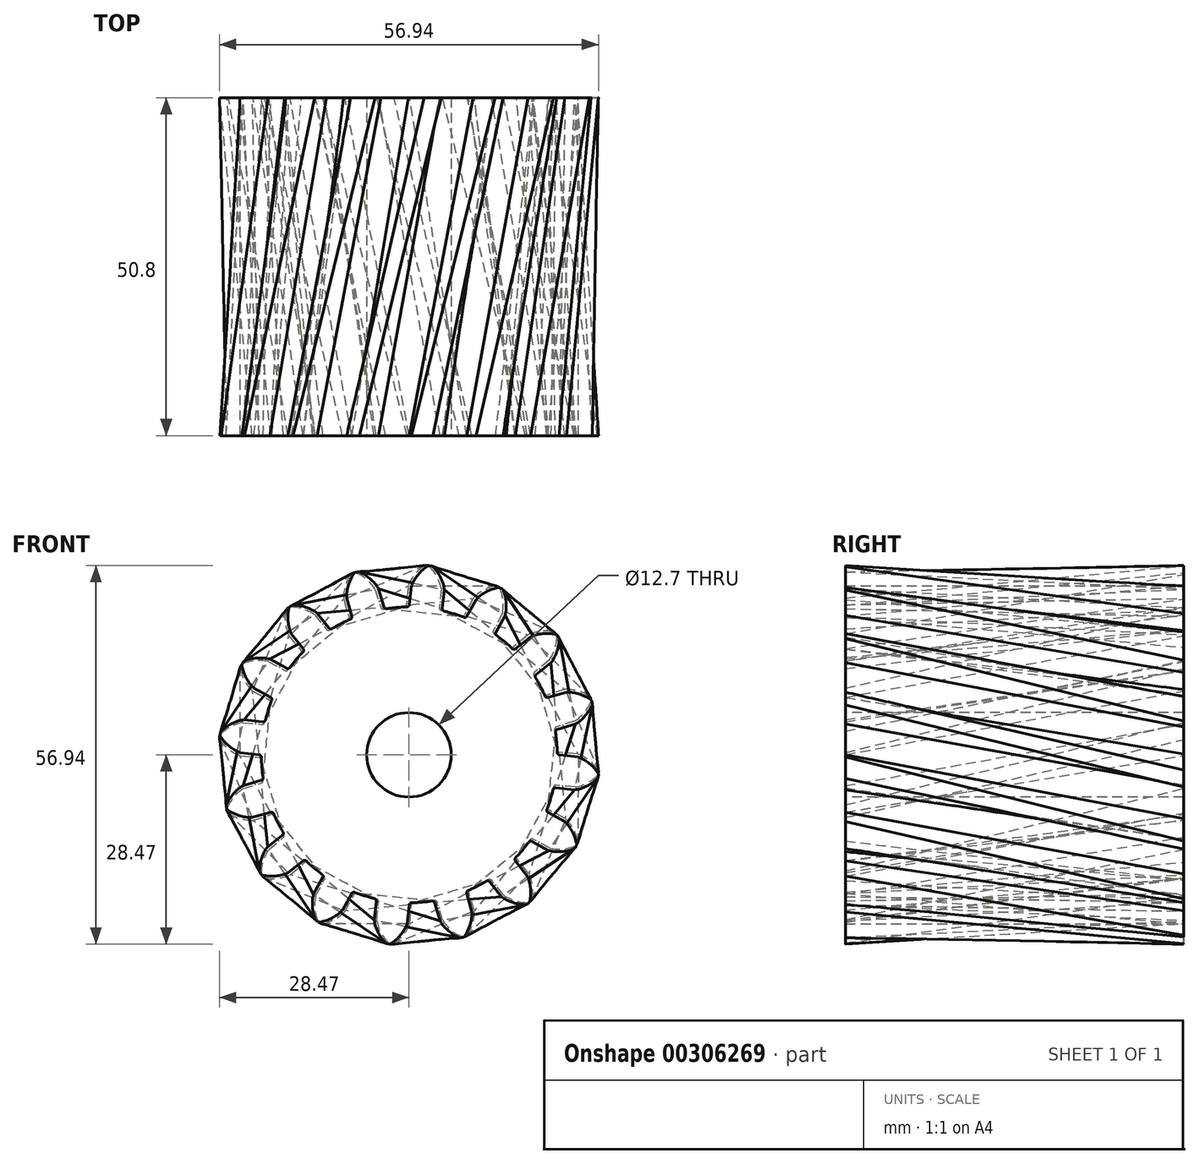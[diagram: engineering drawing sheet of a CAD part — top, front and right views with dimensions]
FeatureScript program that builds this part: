
annotation { "Feature Type Name" : "Feature", "Feature Type Description" : "" }
export const myFeature = defineFeature(function(context is Context, id is Id, definition is map)
    precondition{}
    {
        {
            var Q0;
            Q0=qCreatedBy(makeId("Front.planeOp"),FACE);
            var sketch = newSketch(context, id + "F0", { "sketchPlane" : qUnion([Q0])});
            skArc(sketch, "E0", {"start": v(-0.74, 22.21) * mm, "mid": v(-2.44, 22.1) * mm, "end": v(-4.12, 21.84) * mm});
            skArc(sketch, "E1.trimOffspring", {"start": v(4.85, 24.93) * mm, "mid": v(4.22, 26.77) * mm, "end": v(3.08, 28.32) * mm});
            skLineSegment(sketch, "E2", {"start": v(4.85, 24.93) * mm, "end": v(4.58, 22.1) * mm});
            skLineSegment(sketch, "E3", {"start": v(2.85, 28.43) * mm, "end": v(2.68, 28.45) * mm});
            skArc(sketch, "E4.MirrorCS", {"start": v(-0.11, 25.4) * mm, "mid": v(0.84, 27.08) * mm, "end": v(2.26, 28.4) * mm});
            skLineSegment(sketch, "E5.MirrorCS", {"start": v(2.5, 28.47) * mm, "end": v(2.68, 28.45) * mm});
            skLineSegment(sketch, "E6.MirrorCS", {"start": v(-0.11, 25.4) * mm, "end": v(-0.38, 22.56) * mm});
            skPoint(sketch, "E7.visualSharp", {"position": v(-0.4, 22.22) * mm});
            skArc(sketch, "E7.filletArc", {"start": v(-0.74, 22.21) * mm, "mid": v(-0.5, 22.32) * mm, "end": v(-0.38, 22.56) * mm});
            skPoint(sketch, "E8.visualSharp", {"position": v(4.55, 21.75) * mm});
            skArc(sketch, "E8.filletArc", {"start": v(4.58, 22.1) * mm, "mid": v(4.65, 21.83) * mm, "end": v(4.87, 21.68) * mm});
            skPoint(sketch, "E9.visualSharp", {"position": v(2.98, 28.42) * mm});
            skArc(sketch, "E9.filletArc", {"start": v(3.08, 28.32) * mm, "mid": v(2.97, 28.4) * mm, "end": v(2.85, 28.43) * mm});
            skPoint(sketch, "E10.visualSharp", {"position": v(2.37, 28.48) * mm});
            skArc(sketch, "E10.filletArc", {"start": v(2.5, 28.47) * mm, "mid": v(2.38, 28.45) * mm, "end": v(2.26, 28.4) * mm});
            skLineSegment(sketch, "E11.1.0", {"start": v(-9.82, 23.42) * mm, "end": v(-8.98, 20.7) * mm});
            skPoint(sketch, "E11.1.1", {"position": v(-8.88, 20.37) * mm});
            skLineSegment(sketch, "E11.1.2", {"start": v(-5.06, 24.9) * mm, "end": v(-4.22, 22.16) * mm});
            skPoint(sketch, "E11.1.3", {"position": v(-8.7, 27.22) * mm});
            skArc(sketch, "E11.1.4", {"start": v(-9.82, 23.42) * mm, "mid": v(-9.58, 25.34) * mm, "end": v(-8.78, 27.1) * mm});
            skPoint(sketch, "E11.1.5", {"position": v(-4.12, 21.84) * mm});
            skArc(sketch, "E11.1.6", {"start": v(-5.06, 24.9) * mm, "mid": v(-6.34, 26.34) * mm, "end": v(-8, 27.35) * mm});
            skPoint(sketch, "E11.1.7", {"position": v(-8.12, 27.4) * mm});
            skArc(sketch, "E11.1.8", {"start": v(-8.58, 27.26) * mm, "mid": v(-8.7, 27.2) * mm, "end": v(-8.78, 27.1) * mm});
            skLineSegment(sketch, "E11.1.9", {"start": v(-8.58, 27.26) * mm, "end": v(-8.41, 27.3) * mm});
            skArc(sketch, "E11.1.10", {"start": v(-9.19, 20.24) * mm, "mid": v(-9, 20.43) * mm, "end": v(-8.98, 20.7) * mm});
            skArc(sketch, "E11.1.11", {"start": v(-4.22, 22.16) * mm, "mid": v(-4.06, 21.95) * mm, "end": v(-3.8, 21.9) * mm});
            skLineSegment(sketch, "E11.1.12", {"start": v(-8.25, 27.36) * mm, "end": v(-8.41, 27.3) * mm});
            skArc(sketch, "E11.1.13", {"start": v(-8, 27.35) * mm, "mid": v(-8.12, 27.37) * mm, "end": v(-8.25, 27.36) * mm});
            skLineSegment(sketch, "E11.2.0", {"start": v(-18.04, 17.88) * mm, "end": v(-16.22, 15.68) * mm});
            skPoint(sketch, "E11.2.1", {"position": v(-16, 15.42) * mm});
            skLineSegment(sketch, "E11.2.2", {"start": v(-14.2, 21.06) * mm, "end": v(-12.38, 18.86) * mm});
            skPoint(sketch, "E11.2.3", {"position": v(-18.46, 21.81) * mm});
            skArc(sketch, "E11.2.4", {"start": v(-18.04, 17.88) * mm, "mid": v(-18.55, 19.75) * mm, "end": v(-18.48, 21.68) * mm});
            skPoint(sketch, "E11.2.5", {"position": v(-12.17, 18.6) * mm});
            skArc(sketch, "E11.2.6", {"start": v(-14.2, 21.06) * mm, "mid": v(-15.94, 21.91) * mm, "end": v(-17.85, 22.2) * mm});
            skPoint(sketch, "E11.2.7", {"position": v(-17.99, 22.2) * mm});
            skArc(sketch, "E11.2.8", {"start": v(-18.36, 21.9) * mm, "mid": v(-18.44, 21.8) * mm, "end": v(-18.48, 21.68) * mm});
            skLineSegment(sketch, "E11.2.9", {"start": v(-18.36, 21.9) * mm, "end": v(-18.23, 22.01) * mm});
            skArc(sketch, "E11.2.10", {"start": v(-16.23, 15.18) * mm, "mid": v(-16.13, 15.43) * mm, "end": v(-16.22, 15.68) * mm});
            skArc(sketch, "E11.2.11", {"start": v(-12.38, 18.86) * mm, "mid": v(-12.15, 18.73) * mm, "end": v(-11.89, 18.78) * mm});
            skLineSegment(sketch, "E11.2.12", {"start": v(-18.1, 22.12) * mm, "end": v(-18.23, 22.01) * mm});
            skArc(sketch, "E11.2.13", {"start": v(-17.85, 22.2) * mm, "mid": v(-17.98, 22.18) * mm, "end": v(-18.1, 22.12) * mm});
            skLineSegment(sketch, "E11.3.0", {"start": v(-23.5, 9.62) * mm, "end": v(-20.99, 8.28) * mm});
            skPoint(sketch, "E11.3.1", {"position": v(-20.69, 8.13) * mm});
            skLineSegment(sketch, "E11.3.2", {"start": v(-21.18, 14.02) * mm, "end": v(-18.66, 12.68) * mm});
            skPoint(sketch, "E11.3.3", {"position": v(-25.4, 13.1) * mm});
            skArc(sketch, "E11.3.4", {"start": v(-23.5, 9.62) * mm, "mid": v(-24.7, 11.14) * mm, "end": v(-25.37, 12.96) * mm});
            skPoint(sketch, "E11.3.5", {"position": v(-18.36, 12.53) * mm});
            skArc(sketch, "E11.3.6", {"start": v(-21.18, 14.02) * mm, "mid": v(-23.11, 14.14) * mm, "end": v(-25, 13.68) * mm});
            skPoint(sketch, "E11.3.7", {"position": v(-25.12, 13.63) * mm});
            skArc(sketch, "E11.3.8", {"start": v(-25.34, 13.2) * mm, "mid": v(-25.38, 13.09) * mm, "end": v(-25.37, 12.96) * mm});
            skLineSegment(sketch, "E11.3.9", {"start": v(-25.34, 13.2) * mm, "end": v(-25.26, 13.36) * mm});
            skArc(sketch, "E11.3.10", {"start": v(-20.8, 7.81) * mm, "mid": v(-20.8, 8.08) * mm, "end": v(-20.99, 8.28) * mm});
            skArc(sketch, "E11.3.11", {"start": v(-18.66, 12.68) * mm, "mid": v(-18.4, 12.65) * mm, "end": v(-18.17, 12.8) * mm});
            skLineSegment(sketch, "E11.3.12", {"start": v(-25.18, 13.51) * mm, "end": v(-25.26, 13.36) * mm});
            skArc(sketch, "E11.3.13", {"start": v(-25, 13.68) * mm, "mid": v(-25.1, 13.61) * mm, "end": v(-25.18, 13.51) * mm});
            skLineSegment(sketch, "E11.4.0", {"start": v(-25.4, -0.11) * mm, "end": v(-22.56, -0.38) * mm});
            skPoint(sketch, "E11.4.1", {"position": v(-22.22, -0.4) * mm});
            skLineSegment(sketch, "E11.4.2", {"start": v(-24.93, 4.85) * mm, "end": v(-22.1, 4.58) * mm});
            skPoint(sketch, "E11.4.3", {"position": v(-28.48, 2.37) * mm});
            skArc(sketch, "E11.4.4", {"start": v(-25.4, -0.11) * mm, "mid": v(-27.08, 0.84) * mm, "end": v(-28.4, 2.26) * mm});
            skPoint(sketch, "E11.4.5", {"position": v(-21.75, 4.55) * mm});
            skArc(sketch, "E11.4.6", {"start": v(-24.93, 4.85) * mm, "mid": v(-26.77, 4.22) * mm, "end": v(-28.32, 3.08) * mm});
            skPoint(sketch, "E11.4.7", {"position": v(-28.42, 2.98) * mm});
            skArc(sketch, "E11.4.8", {"start": v(-28.47, 2.5) * mm, "mid": v(-28.45, 2.38) * mm, "end": v(-28.4, 2.26) * mm});
            skLineSegment(sketch, "E11.4.9", {"start": v(-28.47, 2.5) * mm, "end": v(-28.45, 2.68) * mm});
            skArc(sketch, "E11.4.10", {"start": v(-22.21, -0.74) * mm, "mid": v(-22.32, -0.5) * mm, "end": v(-22.56, -0.38) * mm});
            skArc(sketch, "E11.4.11", {"start": v(-22.1, 4.58) * mm, "mid": v(-21.83, 4.65) * mm, "end": v(-21.68, 4.87) * mm});
            skLineSegment(sketch, "E11.4.12", {"start": v(-28.43, 2.85) * mm, "end": v(-28.45, 2.68) * mm});
            skArc(sketch, "E11.4.13", {"start": v(-28.32, 3.08) * mm, "mid": v(-28.4, 2.97) * mm, "end": v(-28.43, 2.85) * mm});
            skLineSegment(sketch, "E11.5.0", {"start": v(-23.42, -9.82) * mm, "end": v(-20.7, -8.98) * mm});
            skPoint(sketch, "E11.5.1", {"position": v(-20.37, -8.88) * mm});
            skLineSegment(sketch, "E11.5.2", {"start": v(-24.9, -5.06) * mm, "end": v(-22.16, -4.22) * mm});
            skPoint(sketch, "E11.5.3", {"position": v(-27.22, -8.7) * mm});
            skArc(sketch, "E11.5.4", {"start": v(-23.42, -9.82) * mm, "mid": v(-25.34, -9.58) * mm, "end": v(-27.1, -8.78) * mm});
            skPoint(sketch, "E11.5.5", {"position": v(-21.84, -4.12) * mm});
            skArc(sketch, "E11.5.6", {"start": v(-24.9, -5.06) * mm, "mid": v(-26.34, -6.34) * mm, "end": v(-27.35, -8) * mm});
            skPoint(sketch, "E11.5.7", {"position": v(-27.4, -8.12) * mm});
            skArc(sketch, "E11.5.8", {"start": v(-27.26, -8.58) * mm, "mid": v(-27.2, -8.7) * mm, "end": v(-27.1, -8.78) * mm});
            skLineSegment(sketch, "E11.5.9", {"start": v(-27.26, -8.58) * mm, "end": v(-27.3, -8.41) * mm});
            skArc(sketch, "E11.5.10", {"start": v(-20.24, -9.19) * mm, "mid": v(-20.43, -9) * mm, "end": v(-20.7, -8.98) * mm});
            skArc(sketch, "E11.5.11", {"start": v(-22.16, -4.22) * mm, "mid": v(-21.95, -4.06) * mm, "end": v(-21.9, -3.8) * mm});
            skLineSegment(sketch, "E11.5.12", {"start": v(-27.36, -8.25) * mm, "end": v(-27.3, -8.41) * mm});
            skArc(sketch, "E11.5.13", {"start": v(-27.35, -8) * mm, "mid": v(-27.37, -8.12) * mm, "end": v(-27.36, -8.25) * mm});
            skLineSegment(sketch, "E11.6.0", {"start": v(-17.88, -18.04) * mm, "end": v(-15.68, -16.22) * mm});
            skPoint(sketch, "E11.6.1", {"position": v(-15.42, -16) * mm});
            skLineSegment(sketch, "E11.6.2", {"start": v(-21.06, -14.2) * mm, "end": v(-18.86, -12.38) * mm});
            skPoint(sketch, "E11.6.3", {"position": v(-21.81, -18.46) * mm});
            skArc(sketch, "E11.6.4", {"start": v(-17.88, -18.04) * mm, "mid": v(-19.75, -18.55) * mm, "end": v(-21.68, -18.48) * mm});
            skPoint(sketch, "E11.6.5", {"position": v(-18.6, -12.17) * mm});
            skArc(sketch, "E11.6.6", {"start": v(-21.06, -14.2) * mm, "mid": v(-21.91, -15.94) * mm, "end": v(-22.2, -17.85) * mm});
            skPoint(sketch, "E11.6.7", {"position": v(-22.2, -17.99) * mm});
            skArc(sketch, "E11.6.8", {"start": v(-21.9, -18.36) * mm, "mid": v(-21.8, -18.44) * mm, "end": v(-21.68, -18.48) * mm});
            skLineSegment(sketch, "E11.6.9", {"start": v(-21.9, -18.36) * mm, "end": v(-22.01, -18.23) * mm});
            skArc(sketch, "E11.6.10", {"start": v(-15.18, -16.23) * mm, "mid": v(-15.43, -16.13) * mm, "end": v(-15.68, -16.22) * mm});
            skArc(sketch, "E11.6.11", {"start": v(-18.86, -12.38) * mm, "mid": v(-18.73, -12.15) * mm, "end": v(-18.78, -11.89) * mm});
            skLineSegment(sketch, "E11.6.12", {"start": v(-22.12, -18.1) * mm, "end": v(-22.01, -18.23) * mm});
            skArc(sketch, "E11.6.13", {"start": v(-22.2, -17.85) * mm, "mid": v(-22.18, -17.98) * mm, "end": v(-22.12, -18.1) * mm});
            skLineSegment(sketch, "E11.7.0", {"start": v(-9.62, -23.5) * mm, "end": v(-8.28, -20.99) * mm});
            skPoint(sketch, "E11.7.1", {"position": v(-8.13, -20.69) * mm});
            skLineSegment(sketch, "E11.7.2", {"start": v(-14.02, -21.18) * mm, "end": v(-12.68, -18.66) * mm});
            skPoint(sketch, "E11.7.3", {"position": v(-13.1, -25.4) * mm});
            skArc(sketch, "E11.7.4", {"start": v(-9.62, -23.5) * mm, "mid": v(-11.14, -24.7) * mm, "end": v(-12.96, -25.37) * mm});
            skPoint(sketch, "E11.7.5", {"position": v(-12.53, -18.36) * mm});
            skArc(sketch, "E11.7.6", {"start": v(-14.02, -21.18) * mm, "mid": v(-14.14, -23.11) * mm, "end": v(-13.68, -25) * mm});
            skPoint(sketch, "E11.7.7", {"position": v(-13.63, -25.12) * mm});
            skArc(sketch, "E11.7.8", {"start": v(-13.2, -25.34) * mm, "mid": v(-13.09, -25.38) * mm, "end": v(-12.96, -25.37) * mm});
            skLineSegment(sketch, "E11.7.9", {"start": v(-13.2, -25.34) * mm, "end": v(-13.36, -25.26) * mm});
            skArc(sketch, "E11.7.10", {"start": v(-7.81, -20.8) * mm, "mid": v(-8.08, -20.8) * mm, "end": v(-8.28, -20.99) * mm});
            skArc(sketch, "E11.7.11", {"start": v(-12.68, -18.66) * mm, "mid": v(-12.65, -18.4) * mm, "end": v(-12.8, -18.17) * mm});
            skLineSegment(sketch, "E11.7.12", {"start": v(-13.51, -25.18) * mm, "end": v(-13.36, -25.26) * mm});
            skArc(sketch, "E11.7.13", {"start": v(-13.68, -25) * mm, "mid": v(-13.61, -25.1) * mm, "end": v(-13.51, -25.18) * mm});
            skLineSegment(sketch, "E11.8.0", {"start": v(0.11, -25.4) * mm, "end": v(0.38, -22.56) * mm});
            skPoint(sketch, "E11.8.1", {"position": v(0.4, -22.22) * mm});
            skLineSegment(sketch, "E11.8.2", {"start": v(-4.85, -24.93) * mm, "end": v(-4.58, -22.1) * mm});
            skPoint(sketch, "E11.8.3", {"position": v(-2.37, -28.48) * mm});
            skArc(sketch, "E11.8.4", {"start": v(0.11, -25.4) * mm, "mid": v(-0.84, -27.08) * mm, "end": v(-2.26, -28.4) * mm});
            skPoint(sketch, "E11.8.5", {"position": v(-4.55, -21.75) * mm});
            skArc(sketch, "E11.8.6", {"start": v(-4.85, -24.93) * mm, "mid": v(-4.22, -26.77) * mm, "end": v(-3.08, -28.32) * mm});
            skPoint(sketch, "E11.8.7", {"position": v(-2.98, -28.42) * mm});
            skArc(sketch, "E11.8.8", {"start": v(-2.5, -28.47) * mm, "mid": v(-2.38, -28.45) * mm, "end": v(-2.26, -28.4) * mm});
            skLineSegment(sketch, "E11.8.9", {"start": v(-2.5, -28.47) * mm, "end": v(-2.68, -28.45) * mm});
            skArc(sketch, "E11.8.10", {"start": v(0.74, -22.21) * mm, "mid": v(0.5, -22.32) * mm, "end": v(0.38, -22.56) * mm});
            skArc(sketch, "E11.8.11", {"start": v(-4.58, -22.1) * mm, "mid": v(-4.65, -21.83) * mm, "end": v(-4.87, -21.68) * mm});
            skLineSegment(sketch, "E11.8.12", {"start": v(-2.85, -28.43) * mm, "end": v(-2.68, -28.45) * mm});
            skArc(sketch, "E11.8.13", {"start": v(-3.08, -28.32) * mm, "mid": v(-2.97, -28.4) * mm, "end": v(-2.85, -28.43) * mm});
            skLineSegment(sketch, "E11.9.0", {"start": v(9.82, -23.42) * mm, "end": v(8.98, -20.7) * mm});
            skPoint(sketch, "E11.9.1", {"position": v(8.88, -20.37) * mm});
            skLineSegment(sketch, "E11.9.2", {"start": v(5.06, -24.9) * mm, "end": v(4.22, -22.16) * mm});
            skPoint(sketch, "E11.9.3", {"position": v(8.7, -27.22) * mm});
            skArc(sketch, "E11.9.4", {"start": v(9.82, -23.42) * mm, "mid": v(9.58, -25.34) * mm, "end": v(8.78, -27.1) * mm});
            skPoint(sketch, "E11.9.5", {"position": v(4.12, -21.84) * mm});
            skArc(sketch, "E11.9.6", {"start": v(5.06, -24.9) * mm, "mid": v(6.34, -26.34) * mm, "end": v(8, -27.35) * mm});
            skPoint(sketch, "E11.9.7", {"position": v(8.12, -27.4) * mm});
            skArc(sketch, "E11.9.8", {"start": v(8.58, -27.26) * mm, "mid": v(8.7, -27.2) * mm, "end": v(8.78, -27.1) * mm});
            skLineSegment(sketch, "E11.9.9", {"start": v(8.58, -27.26) * mm, "end": v(8.41, -27.3) * mm});
            skArc(sketch, "E11.9.10", {"start": v(9.19, -20.24) * mm, "mid": v(9, -20.43) * mm, "end": v(8.98, -20.7) * mm});
            skArc(sketch, "E11.9.11", {"start": v(4.22, -22.16) * mm, "mid": v(4.06, -21.95) * mm, "end": v(3.8, -21.9) * mm});
            skLineSegment(sketch, "E11.9.12", {"start": v(8.25, -27.36) * mm, "end": v(8.41, -27.3) * mm});
            skArc(sketch, "E11.9.13", {"start": v(8, -27.35) * mm, "mid": v(8.12, -27.37) * mm, "end": v(8.25, -27.36) * mm});
            skLineSegment(sketch, "E11.10.0", {"start": v(18.04, -17.88) * mm, "end": v(16.22, -15.68) * mm});
            skPoint(sketch, "E11.10.1", {"position": v(16, -15.42) * mm});
            skLineSegment(sketch, "E11.10.2", {"start": v(14.2, -21.06) * mm, "end": v(12.38, -18.86) * mm});
            skPoint(sketch, "E11.10.3", {"position": v(18.46, -21.81) * mm});
            skArc(sketch, "E11.10.4", {"start": v(18.04, -17.88) * mm, "mid": v(18.55, -19.75) * mm, "end": v(18.48, -21.68) * mm});
            skPoint(sketch, "E11.10.5", {"position": v(12.17, -18.6) * mm});
            skArc(sketch, "E11.10.6", {"start": v(14.2, -21.06) * mm, "mid": v(15.94, -21.91) * mm, "end": v(17.85, -22.2) * mm});
            skPoint(sketch, "E11.10.7", {"position": v(17.99, -22.2) * mm});
            skArc(sketch, "E11.10.8", {"start": v(18.36, -21.9) * mm, "mid": v(18.44, -21.8) * mm, "end": v(18.48, -21.68) * mm});
            skLineSegment(sketch, "E11.10.9", {"start": v(18.36, -21.9) * mm, "end": v(18.23, -22.01) * mm});
            skArc(sketch, "E11.10.10", {"start": v(16.23, -15.18) * mm, "mid": v(16.13, -15.43) * mm, "end": v(16.22, -15.68) * mm});
            skArc(sketch, "E11.10.11", {"start": v(12.38, -18.86) * mm, "mid": v(12.15, -18.73) * mm, "end": v(11.89, -18.78) * mm});
            skLineSegment(sketch, "E11.10.12", {"start": v(18.1, -22.12) * mm, "end": v(18.23, -22.01) * mm});
            skArc(sketch, "E11.10.13", {"start": v(17.85, -22.2) * mm, "mid": v(17.98, -22.18) * mm, "end": v(18.1, -22.12) * mm});
            skLineSegment(sketch, "E11.11.0", {"start": v(23.5, -9.62) * mm, "end": v(20.99, -8.28) * mm});
            skPoint(sketch, "E11.11.1", {"position": v(20.69, -8.13) * mm});
            skLineSegment(sketch, "E11.11.2", {"start": v(21.18, -14.02) * mm, "end": v(18.66, -12.68) * mm});
            skPoint(sketch, "E11.11.3", {"position": v(25.4, -13.1) * mm});
            skArc(sketch, "E11.11.4", {"start": v(23.5, -9.62) * mm, "mid": v(24.7, -11.14) * mm, "end": v(25.37, -12.96) * mm});
            skPoint(sketch, "E11.11.5", {"position": v(18.36, -12.53) * mm});
            skArc(sketch, "E11.11.6", {"start": v(21.18, -14.02) * mm, "mid": v(23.11, -14.14) * mm, "end": v(25, -13.68) * mm});
            skPoint(sketch, "E11.11.7", {"position": v(25.12, -13.63) * mm});
            skArc(sketch, "E11.11.8", {"start": v(25.34, -13.2) * mm, "mid": v(25.38, -13.09) * mm, "end": v(25.37, -12.96) * mm});
            skLineSegment(sketch, "E11.11.9", {"start": v(25.34, -13.2) * mm, "end": v(25.26, -13.36) * mm});
            skArc(sketch, "E11.11.10", {"start": v(20.8, -7.81) * mm, "mid": v(20.8, -8.08) * mm, "end": v(20.99, -8.28) * mm});
            skArc(sketch, "E11.11.11", {"start": v(18.66, -12.68) * mm, "mid": v(18.4, -12.65) * mm, "end": v(18.17, -12.8) * mm});
            skLineSegment(sketch, "E11.11.12", {"start": v(25.18, -13.51) * mm, "end": v(25.26, -13.36) * mm});
            skArc(sketch, "E11.11.13", {"start": v(25, -13.68) * mm, "mid": v(25.1, -13.61) * mm, "end": v(25.18, -13.51) * mm});
            skLineSegment(sketch, "E11.12.0", {"start": v(25.4, 0.11) * mm, "end": v(22.56, 0.38) * mm});
            skPoint(sketch, "E11.12.1", {"position": v(22.22, 0.4) * mm});
            skLineSegment(sketch, "E11.12.2", {"start": v(24.93, -4.85) * mm, "end": v(22.1, -4.58) * mm});
            skPoint(sketch, "E11.12.3", {"position": v(28.48, -2.37) * mm});
            skArc(sketch, "E11.12.4", {"start": v(25.4, 0.11) * mm, "mid": v(27.08, -0.84) * mm, "end": v(28.4, -2.26) * mm});
            skPoint(sketch, "E11.12.5", {"position": v(21.75, -4.55) * mm});
            skArc(sketch, "E11.12.6", {"start": v(24.93, -4.85) * mm, "mid": v(26.77, -4.22) * mm, "end": v(28.32, -3.08) * mm});
            skPoint(sketch, "E11.12.7", {"position": v(28.42, -2.98) * mm});
            skArc(sketch, "E11.12.8", {"start": v(28.47, -2.5) * mm, "mid": v(28.45, -2.38) * mm, "end": v(28.4, -2.26) * mm});
            skLineSegment(sketch, "E11.12.9", {"start": v(28.47, -2.5) * mm, "end": v(28.45, -2.68) * mm});
            skArc(sketch, "E11.12.10", {"start": v(22.21, 0.74) * mm, "mid": v(22.32, 0.5) * mm, "end": v(22.56, 0.38) * mm});
            skArc(sketch, "E11.12.11", {"start": v(22.1, -4.58) * mm, "mid": v(21.83, -4.65) * mm, "end": v(21.68, -4.87) * mm});
            skLineSegment(sketch, "E11.12.12", {"start": v(28.43, -2.85) * mm, "end": v(28.45, -2.68) * mm});
            skArc(sketch, "E11.12.13", {"start": v(28.32, -3.08) * mm, "mid": v(28.4, -2.97) * mm, "end": v(28.43, -2.85) * mm});
            skLineSegment(sketch, "E11.13.0", {"start": v(23.42, 9.82) * mm, "end": v(20.7, 8.98) * mm});
            skPoint(sketch, "E11.13.1", {"position": v(20.37, 8.88) * mm});
            skLineSegment(sketch, "E11.13.2", {"start": v(24.9, 5.06) * mm, "end": v(22.16, 4.22) * mm});
            skPoint(sketch, "E11.13.3", {"position": v(27.22, 8.7) * mm});
            skArc(sketch, "E11.13.4", {"start": v(23.42, 9.82) * mm, "mid": v(25.34, 9.58) * mm, "end": v(27.1, 8.78) * mm});
            skPoint(sketch, "E11.13.5", {"position": v(21.84, 4.12) * mm});
            skArc(sketch, "E11.13.6", {"start": v(24.9, 5.06) * mm, "mid": v(26.34, 6.34) * mm, "end": v(27.35, 8) * mm});
            skPoint(sketch, "E11.13.7", {"position": v(27.4, 8.12) * mm});
            skArc(sketch, "E11.13.8", {"start": v(27.26, 8.58) * mm, "mid": v(27.2, 8.7) * mm, "end": v(27.1, 8.78) * mm});
            skLineSegment(sketch, "E11.13.9", {"start": v(27.26, 8.58) * mm, "end": v(27.3, 8.41) * mm});
            skArc(sketch, "E11.13.10", {"start": v(20.24, 9.19) * mm, "mid": v(20.43, 9) * mm, "end": v(20.7, 8.98) * mm});
            skArc(sketch, "E11.13.11", {"start": v(22.16, 4.22) * mm, "mid": v(21.95, 4.06) * mm, "end": v(21.9, 3.8) * mm});
            skLineSegment(sketch, "E11.13.12", {"start": v(27.36, 8.25) * mm, "end": v(27.3, 8.41) * mm});
            skArc(sketch, "E11.13.13", {"start": v(27.35, 8) * mm, "mid": v(27.37, 8.12) * mm, "end": v(27.36, 8.25) * mm});
            skLineSegment(sketch, "E11.14.0", {"start": v(17.88, 18.04) * mm, "end": v(15.68, 16.22) * mm});
            skPoint(sketch, "E11.14.1", {"position": v(15.42, 16) * mm});
            skLineSegment(sketch, "E11.14.2", {"start": v(21.06, 14.2) * mm, "end": v(18.86, 12.38) * mm});
            skPoint(sketch, "E11.14.3", {"position": v(21.81, 18.46) * mm});
            skArc(sketch, "E11.14.4", {"start": v(17.88, 18.04) * mm, "mid": v(19.75, 18.55) * mm, "end": v(21.68, 18.48) * mm});
            skPoint(sketch, "E11.14.5", {"position": v(18.6, 12.17) * mm});
            skArc(sketch, "E11.14.6", {"start": v(21.06, 14.2) * mm, "mid": v(21.91, 15.94) * mm, "end": v(22.2, 17.85) * mm});
            skPoint(sketch, "E11.14.7", {"position": v(22.2, 17.99) * mm});
            skArc(sketch, "E11.14.8", {"start": v(21.9, 18.36) * mm, "mid": v(21.8, 18.44) * mm, "end": v(21.68, 18.48) * mm});
            skLineSegment(sketch, "E11.14.9", {"start": v(21.9, 18.36) * mm, "end": v(22.01, 18.23) * mm});
            skArc(sketch, "E11.14.10", {"start": v(15.18, 16.23) * mm, "mid": v(15.43, 16.13) * mm, "end": v(15.68, 16.22) * mm});
            skArc(sketch, "E11.14.11", {"start": v(18.86, 12.38) * mm, "mid": v(18.73, 12.15) * mm, "end": v(18.78, 11.89) * mm});
            skLineSegment(sketch, "E11.14.12", {"start": v(22.12, 18.1) * mm, "end": v(22.01, 18.23) * mm});
            skArc(sketch, "E11.14.13", {"start": v(22.2, 17.85) * mm, "mid": v(22.18, 17.98) * mm, "end": v(22.12, 18.1) * mm});
            skLineSegment(sketch, "E11.15.0", {"start": v(9.62, 23.5) * mm, "end": v(8.28, 20.99) * mm});
            skPoint(sketch, "E11.15.1", {"position": v(8.13, 20.69) * mm});
            skLineSegment(sketch, "E11.15.2", {"start": v(14.02, 21.18) * mm, "end": v(12.68, 18.66) * mm});
            skPoint(sketch, "E11.15.3", {"position": v(13.1, 25.4) * mm});
            skArc(sketch, "E11.15.4", {"start": v(9.62, 23.5) * mm, "mid": v(11.14, 24.7) * mm, "end": v(12.96, 25.37) * mm});
            skPoint(sketch, "E11.15.5", {"position": v(12.53, 18.36) * mm});
            skArc(sketch, "E11.15.6", {"start": v(14.02, 21.18) * mm, "mid": v(14.14, 23.11) * mm, "end": v(13.68, 25) * mm});
            skPoint(sketch, "E11.15.7", {"position": v(13.63, 25.12) * mm});
            skArc(sketch, "E11.15.8", {"start": v(13.2, 25.34) * mm, "mid": v(13.09, 25.38) * mm, "end": v(12.96, 25.37) * mm});
            skLineSegment(sketch, "E11.15.9", {"start": v(13.2, 25.34) * mm, "end": v(13.36, 25.26) * mm});
            skArc(sketch, "E11.15.10", {"start": v(7.81, 20.8) * mm, "mid": v(8.08, 20.8) * mm, "end": v(8.28, 20.99) * mm});
            skArc(sketch, "E11.15.11", {"start": v(12.68, 18.66) * mm, "mid": v(12.65, 18.4) * mm, "end": v(12.8, 18.17) * mm});
            skLineSegment(sketch, "E11.15.12", {"start": v(13.51, 25.18) * mm, "end": v(13.36, 25.26) * mm});
            skArc(sketch, "E11.15.13", {"start": v(13.68, 25) * mm, "mid": v(13.61, 25.1) * mm, "end": v(13.51, 25.18) * mm});
            skArc(sketch, "E12.trimOffspring", {"start": v(8.13, 20.69) * mm, "mid": v(6.52, 21.25) * mm, "end": v(4.87, 21.68) * mm});
            skArc(sketch, "E13.trimOffspring", {"start": v(-8.88, 20.37) * mm, "mid": v(-10.56, 19.55) * mm, "end": v(-12.17, 18.6) * mm});
            skArc(sketch, "E14.trimOffspring", {"start": v(15.42, 16) * mm, "mid": v(14.02, 17.24) * mm, "end": v(12.53, 18.36) * mm});
            skArc(sketch, "E15.trimOffspring", {"start": v(-16, 15.42) * mm, "mid": v(-17.24, 14.02) * mm, "end": v(-18.36, 12.53) * mm});
            skArc(sketch, "E16.trimOffspring", {"start": v(-20.69, 8.13) * mm, "mid": v(-21.25, 6.52) * mm, "end": v(-21.68, 4.87) * mm});
            skArc(sketch, "E17.trimOffspring", {"start": v(20.37, 8.88) * mm, "mid": v(19.55, 10.56) * mm, "end": v(18.6, 12.17) * mm});
            skArc(sketch, "E18.trimOffspring", {"start": v(22.22, 0.4) * mm, "mid": v(22.1, 2.27) * mm, "end": v(21.84, 4.12) * mm});
            skArc(sketch, "E19.trimOffspring", {"start": v(-22.22, -0.4) * mm, "mid": v(-22.12, -2.1) * mm, "end": v(-21.9, -3.8) * mm});
            skArc(sketch, "E20.trimOffspring", {"start": v(-20.37, -8.88) * mm, "mid": v(-19.55, -10.56) * mm, "end": v(-18.6, -12.17) * mm});
            skArc(sketch, "E21.trimOffspring", {"start": v(-8.13, -20.69) * mm, "mid": v(-6.36, -21.3) * mm, "end": v(-4.55, -21.75) * mm});
            skArc(sketch, "E22.trimOffspring", {"start": v(-15.42, -16) * mm, "mid": v(-14.02, -17.24) * mm, "end": v(-12.53, -18.36) * mm});
            skArc(sketch, "E23.trimOffspring", {"start": v(0.4, -22.22) * mm, "mid": v(2.1, -22.12) * mm, "end": v(3.8, -21.9) * mm});
            skArc(sketch, "E24.trimOffspring", {"start": v(8.88, -20.37) * mm, "mid": v(10.41, -19.63) * mm, "end": v(11.89, -18.78) * mm});
            skArc(sketch, "E25.trimOffspring", {"start": v(16, -15.42) * mm, "mid": v(17.24, -14.02) * mm, "end": v(18.36, -12.53) * mm});
            skArc(sketch, "E26.trimOffspring", {"start": v(20.69, -8.13) * mm, "mid": v(21.3, -6.36) * mm, "end": v(21.75, -4.55) * mm});
            skSolve(sketch);
        }
        {
            var Q0;
            Q0=makeQuery(id+"F0.imprint","IMPRINT",FACE,{"disambiguationData":[TD([[makeQuery(id+"F0.imprint","IMPRINT",EDGE,{"derivedFrom":sQuery(id+"F0.wireOp",EDGE,"E1.trimOffspring")}),1.0]])]});
            cPlane(context, id + "F1", {"entities" : qUnion([Q0]), "cplaneType" : CPlaneType.OFFSET, "offset" : 50.8 * mm, "width" : 152.4 * mm, "height" : 152.4 * mm});
        }
        {
            var Q0;
            Q0=qCreatedBy(id+"F1.planeOp",FACE);
            var sketch = newSketch(context, id + "F2", { "sketchPlane" : qUnion([Q0])});
            skArc(sketch, "E27", {"start": v(-15.92, 15.46) * mm, "mid": v(-17.06, 14.2) * mm, "end": v(-18.1, 12.85) * mm});
            skArc(sketch, "E28.trimOffspring", {"start": v(-13.79, 21.3) * mm, "mid": v(-15.5, 22.19) * mm, "end": v(-17.42, 22.51) * mm});
            skLineSegment(sketch, "E29", {"start": v(-13.79, 21.3) * mm, "end": v(-12, 19.07) * mm});
            skLineSegment(sketch, "E30", {"start": v(-17.66, 22.43) * mm, "end": v(-17.8, 22.33) * mm});
            skArc(sketch, "E31.MirrorCS", {"start": v(-17.68, 18.2) * mm, "mid": v(-18.16, 20.07) * mm, "end": v(-18.06, 22) * mm});
            skLineSegment(sketch, "E32.MirrorCS", {"start": v(-17.92, 22.22) * mm, "end": v(-17.8, 22.33) * mm});
            skLineSegment(sketch, "E33.MirrorCS", {"start": v(-17.68, 18.2) * mm, "end": v(-15.9, 15.96) * mm});
            skPoint(sketch, "E34.visualSharp", {"position": v(-15.68, 15.7) * mm});
            skArc(sketch, "E34.filletArc", {"start": v(-15.92, 15.46) * mm, "mid": v(-15.81, 15.7) * mm, "end": v(-15.9, 15.96) * mm});
            skPoint(sketch, "E35.visualSharp", {"position": v(-11.8, 18.8) * mm});
            skArc(sketch, "E35.filletArc", {"start": v(-12, 19.07) * mm, "mid": v(-11.77, 18.93) * mm, "end": v(-11.5, 18.98) * mm});
            skPoint(sketch, "E36.visualSharp", {"position": v(-17.55, 22.51) * mm});
            skArc(sketch, "E36.filletArc", {"start": v(-17.42, 22.51) * mm, "mid": v(-17.54, 22.5) * mm, "end": v(-17.66, 22.43) * mm});
            skPoint(sketch, "E37.visualSharp", {"position": v(-18.03, 22.13) * mm});
            skArc(sketch, "E37.filletArc", {"start": v(-17.92, 22.22) * mm, "mid": v(-18, 22.12) * mm, "end": v(-18.06, 22) * mm});
            skLineSegment(sketch, "E38.1.0", {"start": v(-23.3, 10.03) * mm, "end": v(-20.8, 8.65) * mm});
            skPoint(sketch, "E38.1.1", {"position": v(-20.5, 8.48) * mm});
            skLineSegment(sketch, "E38.1.2", {"start": v(-20.89, 14.39) * mm, "end": v(-18.39, 13) * mm});
            skPoint(sketch, "E38.1.3", {"position": v(-25.12, 13.53) * mm});
            skArc(sketch, "E38.1.4", {"start": v(-23.3, 10.03) * mm, "mid": v(-24.45, 11.57) * mm, "end": v(-25.1, 13.4) * mm});
            skPoint(sketch, "E38.1.5", {"position": v(-18.1, 12.85) * mm});
            skArc(sketch, "E38.1.6", {"start": v(-20.89, 14.39) * mm, "mid": v(-22.81, 14.55) * mm, "end": v(-24.7, 14.12) * mm});
            skPoint(sketch, "E38.1.7", {"position": v(-24.83, 14.06) * mm});
            skArc(sketch, "E38.1.8", {"start": v(-25.06, 13.65) * mm, "mid": v(-25.1, 13.53) * mm, "end": v(-25.1, 13.4) * mm});
            skLineSegment(sketch, "E38.1.9", {"start": v(-25.06, 13.65) * mm, "end": v(-24.98, 13.8) * mm});
            skArc(sketch, "E38.1.10", {"start": v(-20.62, 8.17) * mm, "mid": v(-20.62, 8.44) * mm, "end": v(-20.8, 8.65) * mm});
            skArc(sketch, "E38.1.11", {"start": v(-18.39, 13) * mm, "mid": v(-18.12, 12.97) * mm, "end": v(-17.9, 13.12) * mm});
            skLineSegment(sketch, "E38.1.12", {"start": v(-24.9, 13.95) * mm, "end": v(-24.98, 13.8) * mm});
            skArc(sketch, "E38.1.13", {"start": v(-24.7, 14.12) * mm, "mid": v(-24.81, 14.05) * mm, "end": v(-24.9, 13.95) * mm});
            skLineSegment(sketch, "E38.2.0", {"start": v(-25.35, 0.33) * mm, "end": v(-22.51, 0.02) * mm});
            skPoint(sketch, "E38.2.1", {"position": v(-22.18, -0.02) * mm});
            skLineSegment(sketch, "E38.2.2", {"start": v(-24.8, 5.28) * mm, "end": v(-21.96, 4.96) * mm});
            skPoint(sketch, "E38.2.3", {"position": v(-28.38, 2.87) * mm});
            skArc(sketch, "E38.2.4", {"start": v(-25.35, 0.33) * mm, "mid": v(-27.02, 1.32) * mm, "end": v(-28.31, 2.76) * mm});
            skPoint(sketch, "E38.2.5", {"position": v(-21.63, 4.93) * mm});
            skArc(sketch, "E38.2.6", {"start": v(-24.8, 5.28) * mm, "mid": v(-26.64, 4.69) * mm, "end": v(-28.22, 3.57) * mm});
            skPoint(sketch, "E38.2.7", {"position": v(-28.32, 3.47) * mm});
            skArc(sketch, "E38.2.8", {"start": v(-28.37, 3) * mm, "mid": v(-28.36, 2.87) * mm, "end": v(-28.31, 2.76) * mm});
            skLineSegment(sketch, "E38.2.9", {"start": v(-28.37, 3) * mm, "end": v(-28.35, 3.17) * mm});
            skArc(sketch, "E38.2.10", {"start": v(-22.18, -0.36) * mm, "mid": v(-22.27, -0.1) * mm, "end": v(-22.51, 0.02) * mm});
            skArc(sketch, "E38.2.11", {"start": v(-21.96, 4.96) * mm, "mid": v(-21.7, 5.03) * mm, "end": v(-21.55, 5.25) * mm});
            skLineSegment(sketch, "E38.2.12", {"start": v(-28.33, 3.34) * mm, "end": v(-28.35, 3.17) * mm});
            skArc(sketch, "E38.2.13", {"start": v(-28.22, 3.57) * mm, "mid": v(-28.3, 3.47) * mm, "end": v(-28.33, 3.34) * mm});
            skLineSegment(sketch, "E38.3.0", {"start": v(-23.55, -9.41) * mm, "end": v(-20.8, -8.62) * mm});
            skPoint(sketch, "E38.3.1", {"position": v(-20.48, -8.53) * mm});
            skLineSegment(sketch, "E38.3.2", {"start": v(-24.93, -4.63) * mm, "end": v(-22.19, -3.84) * mm});
            skPoint(sketch, "E38.3.3", {"position": v(-27.32, -8.23) * mm});
            skArc(sketch, "E38.3.4", {"start": v(-23.55, -9.41) * mm, "mid": v(-25.46, -9.14) * mm, "end": v(-27.2, -8.3) * mm});
            skPoint(sketch, "E38.3.5", {"position": v(-21.86, -3.74) * mm});
            skArc(sketch, "E38.3.6", {"start": v(-24.93, -4.63) * mm, "mid": v(-26.4, -5.88) * mm, "end": v(-27.43, -7.52) * mm});
            skPoint(sketch, "E38.3.7", {"position": v(-27.49, -7.64) * mm});
            skArc(sketch, "E38.3.8", {"start": v(-27.36, -8.1) * mm, "mid": v(-27.3, -8.22) * mm, "end": v(-27.2, -8.3) * mm});
            skLineSegment(sketch, "E38.3.9", {"start": v(-27.36, -8.1) * mm, "end": v(-27.4, -7.94) * mm});
            skArc(sketch, "E38.3.10", {"start": v(-20.35, -8.83) * mm, "mid": v(-20.53, -8.64) * mm, "end": v(-20.8, -8.62) * mm});
            skArc(sketch, "E38.3.11", {"start": v(-22.19, -3.84) * mm, "mid": v(-21.97, -3.67) * mm, "end": v(-21.92, -3.41) * mm});
            skLineSegment(sketch, "E38.3.12", {"start": v(-27.45, -7.77) * mm, "end": v(-27.4, -7.94) * mm});
            skArc(sketch, "E38.3.13", {"start": v(-27.43, -7.52) * mm, "mid": v(-27.46, -7.64) * mm, "end": v(-27.45, -7.77) * mm});
            skLineSegment(sketch, "E38.4.0", {"start": v(-18.15, -17.72) * mm, "end": v(-15.92, -15.94) * mm});
            skPoint(sketch, "E38.4.1", {"position": v(-15.65, -15.73) * mm});
            skLineSegment(sketch, "E38.4.2", {"start": v(-21.26, -13.83) * mm, "end": v(-19.03, -12.05) * mm});
            skPoint(sketch, "E38.4.3", {"position": v(-22.09, -18.07) * mm});
            skArc(sketch, "E38.4.4", {"start": v(-18.15, -17.72) * mm, "mid": v(-20.02, -18.2) * mm, "end": v(-21.95, -18.1) * mm});
            skPoint(sketch, "E38.4.5", {"position": v(-18.76, -11.84) * mm});
            skArc(sketch, "E38.4.6", {"start": v(-21.26, -13.83) * mm, "mid": v(-22.14, -15.55) * mm, "end": v(-22.47, -17.46) * mm});
            skPoint(sketch, "E38.4.7", {"position": v(-22.47, -17.6) * mm});
            skArc(sketch, "E38.4.8", {"start": v(-22.17, -17.97) * mm, "mid": v(-22.07, -18.06) * mm, "end": v(-21.95, -18.1) * mm});
            skLineSegment(sketch, "E38.4.9", {"start": v(-22.17, -17.97) * mm, "end": v(-22.28, -17.84) * mm});
            skArc(sketch, "E38.4.10", {"start": v(-15.41, -15.97) * mm, "mid": v(-15.66, -15.86) * mm, "end": v(-15.92, -15.94) * mm});
            skArc(sketch, "E38.4.11", {"start": v(-19.03, -12.05) * mm, "mid": v(-18.89, -11.82) * mm, "end": v(-18.94, -11.56) * mm});
            skLineSegment(sketch, "E38.4.12", {"start": v(-22.38, -17.7) * mm, "end": v(-22.28, -17.84) * mm});
            skArc(sketch, "E38.4.13", {"start": v(-22.47, -17.46) * mm, "mid": v(-22.45, -17.59) * mm, "end": v(-22.38, -17.7) * mm});
            skLineSegment(sketch, "E38.5.0", {"start": v(-9.98, -23.34) * mm, "end": v(-8.6, -20.84) * mm});
            skPoint(sketch, "E38.5.1", {"position": v(-8.44, -20.54) * mm});
            skLineSegment(sketch, "E38.5.2", {"start": v(-14.34, -20.93) * mm, "end": v(-12.96, -18.43) * mm});
            skPoint(sketch, "E38.5.3", {"position": v(-13.49, -25.17) * mm});
            skArc(sketch, "E38.5.4", {"start": v(-9.98, -23.34) * mm, "mid": v(-11.53, -24.5) * mm, "end": v(-13.35, -25.14) * mm});
            skPoint(sketch, "E38.5.5", {"position": v(-12.8, -18.14) * mm});
            skArc(sketch, "E38.5.6", {"start": v(-14.34, -20.93) * mm, "mid": v(-14.5, -22.86) * mm, "end": v(-14.07, -24.75) * mm});
            skPoint(sketch, "E38.5.7", {"position": v(-14.02, -24.87) * mm});
            skArc(sketch, "E38.5.8", {"start": v(-13.6, -25.1) * mm, "mid": v(-13.48, -25.15) * mm, "end": v(-13.35, -25.14) * mm});
            skLineSegment(sketch, "E38.5.9", {"start": v(-13.6, -25.1) * mm, "end": v(-13.75, -25.02) * mm});
            skArc(sketch, "E38.5.10", {"start": v(-8.13, -20.67) * mm, "mid": v(-8.4, -20.66) * mm, "end": v(-8.6, -20.84) * mm});
            skArc(sketch, "E38.5.11", {"start": v(-12.96, -18.43) * mm, "mid": v(-12.92, -18.17) * mm, "end": v(-13.07, -17.94) * mm});
            skLineSegment(sketch, "E38.5.12", {"start": v(-13.9, -24.94) * mm, "end": v(-13.75, -25.02) * mm});
            skArc(sketch, "E38.5.13", {"start": v(-14.07, -24.75) * mm, "mid": v(-14, -24.86) * mm, "end": v(-13.9, -24.94) * mm});
            skLineSegment(sketch, "E38.6.0", {"start": v(-0.29, -25.4) * mm, "end": v(0.03, -22.56) * mm});
            skPoint(sketch, "E38.6.1", {"position": v(0.07, -22.22) * mm});
            skLineSegment(sketch, "E38.6.2", {"start": v(-5.23, -24.84) * mm, "end": v(-4.92, -22) * mm});
            skPoint(sketch, "E38.6.3", {"position": v(-2.82, -28.43) * mm});
            skArc(sketch, "E38.6.4", {"start": v(-0.29, -25.4) * mm, "mid": v(-1.27, -27.06) * mm, "end": v(-2.7, -28.36) * mm});
            skPoint(sketch, "E38.6.5", {"position": v(-4.88, -21.67) * mm});
            skArc(sketch, "E38.6.6", {"start": v(-5.23, -24.84) * mm, "mid": v(-4.64, -26.69) * mm, "end": v(-3.52, -28.27) * mm});
            skPoint(sketch, "E38.6.7", {"position": v(-3.43, -28.36) * mm});
            skArc(sketch, "E38.6.8", {"start": v(-2.96, -28.42) * mm, "mid": v(-2.83, -28.4) * mm, "end": v(-2.7, -28.36) * mm});
            skLineSegment(sketch, "E38.6.9", {"start": v(-2.96, -28.42) * mm, "end": v(-3.13, -28.4) * mm});
            skArc(sketch, "E38.6.10", {"start": v(0.4, -22.22) * mm, "mid": v(0.15, -22.32) * mm, "end": v(0.03, -22.56) * mm});
            skArc(sketch, "E38.6.11", {"start": v(-4.92, -22) * mm, "mid": v(-4.98, -21.75) * mm, "end": v(-5.2, -21.6) * mm});
            skLineSegment(sketch, "E38.6.12", {"start": v(-3.3, -28.38) * mm, "end": v(-3.13, -28.4) * mm});
            skArc(sketch, "E38.6.13", {"start": v(-3.52, -28.27) * mm, "mid": v(-3.42, -28.34) * mm, "end": v(-3.3, -28.38) * mm});
            skLineSegment(sketch, "E38.7.0", {"start": v(9.46, -23.6) * mm, "end": v(8.67, -20.85) * mm});
            skPoint(sketch, "E38.7.1", {"position": v(8.57, -20.52) * mm});
            skLineSegment(sketch, "E38.7.2", {"start": v(4.68, -24.97) * mm, "end": v(3.88, -22.23) * mm});
            skPoint(sketch, "E38.7.3", {"position": v(8.27, -27.36) * mm});
            skArc(sketch, "E38.7.4", {"start": v(9.46, -23.6) * mm, "mid": v(9.19, -25.5) * mm, "end": v(8.35, -27.25) * mm});
            skPoint(sketch, "E38.7.5", {"position": v(3.79, -21.9) * mm});
            skArc(sketch, "E38.7.6", {"start": v(4.68, -24.97) * mm, "mid": v(5.93, -26.45) * mm, "end": v(7.56, -27.48) * mm});
            skPoint(sketch, "E38.7.7", {"position": v(7.7, -27.53) * mm});
            skArc(sketch, "E38.7.8", {"start": v(8.15, -27.4) * mm, "mid": v(8.26, -27.35) * mm, "end": v(8.35, -27.25) * mm});
            skLineSegment(sketch, "E38.7.9", {"start": v(8.15, -27.4) * mm, "end": v(7.98, -27.45) * mm});
            skArc(sketch, "E38.7.10", {"start": v(8.88, -20.4) * mm, "mid": v(8.69, -20.58) * mm, "end": v(8.67, -20.85) * mm});
            skArc(sketch, "E38.7.11", {"start": v(3.88, -22.23) * mm, "mid": v(3.72, -22.02) * mm, "end": v(3.46, -21.96) * mm});
            skLineSegment(sketch, "E38.7.12", {"start": v(7.82, -27.5) * mm, "end": v(7.98, -27.45) * mm});
            skArc(sketch, "E38.7.13", {"start": v(7.56, -27.48) * mm, "mid": v(7.69, -27.51) * mm, "end": v(7.82, -27.5) * mm});
            skLineSegment(sketch, "E38.8.0", {"start": v(17.77, -18.2) * mm, "end": v(15.99, -15.96) * mm});
            skPoint(sketch, "E38.8.1", {"position": v(15.78, -15.7) * mm});
            skLineSegment(sketch, "E38.8.2", {"start": v(13.88, -21.3) * mm, "end": v(12.1, -19.07) * mm});
            skPoint(sketch, "E38.8.3", {"position": v(18.12, -22.13) * mm});
            skArc(sketch, "E38.8.4", {"start": v(17.77, -18.2) * mm, "mid": v(18.25, -20.07) * mm, "end": v(18.15, -22) * mm});
            skPoint(sketch, "E38.8.5", {"position": v(11.89, -18.8) * mm});
            skArc(sketch, "E38.8.6", {"start": v(13.88, -21.3) * mm, "mid": v(15.6, -22.19) * mm, "end": v(17.5, -22.51) * mm});
            skPoint(sketch, "E38.8.7", {"position": v(17.65, -22.51) * mm});
            skArc(sketch, "E38.8.8", {"start": v(18.02, -22.22) * mm, "mid": v(18.1, -22.12) * mm, "end": v(18.15, -22) * mm});
            skLineSegment(sketch, "E38.8.9", {"start": v(18.02, -22.22) * mm, "end": v(17.88, -22.33) * mm});
            skArc(sketch, "E38.8.10", {"start": v(16.01, -15.46) * mm, "mid": v(15.9, -15.7) * mm, "end": v(15.99, -15.96) * mm});
            skArc(sketch, "E38.8.11", {"start": v(12.1, -19.07) * mm, "mid": v(11.87, -18.93) * mm, "end": v(11.6, -18.98) * mm});
            skLineSegment(sketch, "E38.8.12", {"start": v(17.75, -22.43) * mm, "end": v(17.88, -22.33) * mm});
            skArc(sketch, "E38.8.13", {"start": v(17.5, -22.51) * mm, "mid": v(17.64, -22.5) * mm, "end": v(17.75, -22.43) * mm});
            skLineSegment(sketch, "E38.9.0", {"start": v(23.38, -10.03) * mm, "end": v(20.88, -8.65) * mm});
            skPoint(sketch, "E38.9.1", {"position": v(20.59, -8.48) * mm});
            skLineSegment(sketch, "E38.9.2", {"start": v(20.98, -14.39) * mm, "end": v(18.48, -13) * mm});
            skPoint(sketch, "E38.9.3", {"position": v(25.21, -13.53) * mm});
            skArc(sketch, "E38.9.4", {"start": v(23.38, -10.03) * mm, "mid": v(24.55, -11.57) * mm, "end": v(25.2, -13.4) * mm});
            skPoint(sketch, "E38.9.5", {"position": v(18.18, -12.85) * mm});
            skArc(sketch, "E38.9.6", {"start": v(20.98, -14.39) * mm, "mid": v(22.9, -14.55) * mm, "end": v(24.8, -14.12) * mm});
            skPoint(sketch, "E38.9.7", {"position": v(24.92, -14.06) * mm});
            skArc(sketch, "E38.9.8", {"start": v(25.15, -13.65) * mm, "mid": v(25.2, -13.53) * mm, "end": v(25.2, -13.4) * mm});
            skLineSegment(sketch, "E38.9.9", {"start": v(25.15, -13.65) * mm, "end": v(25.07, -13.8) * mm});
            skArc(sketch, "E38.9.10", {"start": v(20.71, -8.17) * mm, "mid": v(20.7, -8.44) * mm, "end": v(20.88, -8.65) * mm});
            skArc(sketch, "E38.9.11", {"start": v(18.48, -13) * mm, "mid": v(18.21, -12.97) * mm, "end": v(17.99, -13.12) * mm});
            skLineSegment(sketch, "E38.9.12", {"start": v(24.99, -13.95) * mm, "end": v(25.07, -13.8) * mm});
            skArc(sketch, "E38.9.13", {"start": v(24.8, -14.12) * mm, "mid": v(24.9, -14.05) * mm, "end": v(24.99, -13.95) * mm});
            skLineSegment(sketch, "E38.10.0", {"start": v(25.44, -0.33) * mm, "end": v(22.6, -0.02) * mm});
            skPoint(sketch, "E38.10.1", {"position": v(22.27, 0.02) * mm});
            skLineSegment(sketch, "E38.10.2", {"start": v(24.9, -5.28) * mm, "end": v(22.05, -4.96) * mm});
            skPoint(sketch, "E38.10.3", {"position": v(28.48, -2.87) * mm});
            skArc(sketch, "E38.10.4", {"start": v(25.44, -0.33) * mm, "mid": v(27.11, -1.32) * mm, "end": v(28.4, -2.76) * mm});
            skPoint(sketch, "E38.10.5", {"position": v(21.72, -4.93) * mm});
            skArc(sketch, "E38.10.6", {"start": v(24.9, -5.28) * mm, "mid": v(26.73, -4.69) * mm, "end": v(28.31, -3.57) * mm});
            skPoint(sketch, "E38.10.7", {"position": v(28.4, -3.47) * mm});
            skArc(sketch, "E38.10.8", {"start": v(28.46, -3) * mm, "mid": v(28.45, -2.87) * mm, "end": v(28.4, -2.76) * mm});
            skLineSegment(sketch, "E38.10.9", {"start": v(28.46, -3) * mm, "end": v(28.45, -3.17) * mm});
            skArc(sketch, "E38.10.10", {"start": v(22.27, 0.36) * mm, "mid": v(22.37, 0.1) * mm, "end": v(22.6, -0.02) * mm});
            skArc(sketch, "E38.10.11", {"start": v(22.05, -4.96) * mm, "mid": v(21.8, -5.03) * mm, "end": v(21.64, -5.25) * mm});
            skLineSegment(sketch, "E38.10.12", {"start": v(28.43, -3.34) * mm, "end": v(28.45, -3.17) * mm});
            skArc(sketch, "E38.10.13", {"start": v(28.31, -3.57) * mm, "mid": v(28.39, -3.47) * mm, "end": v(28.43, -3.34) * mm});
            skLineSegment(sketch, "E38.11.0", {"start": v(23.64, 9.41) * mm, "end": v(20.9, 8.62) * mm});
            skPoint(sketch, "E38.11.1", {"position": v(20.57, 8.53) * mm});
            skLineSegment(sketch, "E38.11.2", {"start": v(25.02, 4.63) * mm, "end": v(22.28, 3.84) * mm});
            skPoint(sketch, "E38.11.3", {"position": v(27.41, 8.23) * mm});
            skArc(sketch, "E38.11.4", {"start": v(23.64, 9.41) * mm, "mid": v(25.55, 9.14) * mm, "end": v(27.3, 8.3) * mm});
            skPoint(sketch, "E38.11.5", {"position": v(21.95, 3.74) * mm});
            skArc(sketch, "E38.11.6", {"start": v(25.02, 4.63) * mm, "mid": v(26.5, 5.88) * mm, "end": v(27.53, 7.52) * mm});
            skPoint(sketch, "E38.11.7", {"position": v(27.58, 7.64) * mm});
            skArc(sketch, "E38.11.8", {"start": v(27.45, 8.1) * mm, "mid": v(27.4, 8.22) * mm, "end": v(27.3, 8.3) * mm});
            skLineSegment(sketch, "E38.11.9", {"start": v(27.45, 8.1) * mm, "end": v(27.5, 7.94) * mm});
            skArc(sketch, "E38.11.10", {"start": v(20.44, 8.83) * mm, "mid": v(20.63, 8.64) * mm, "end": v(20.9, 8.62) * mm});
            skArc(sketch, "E38.11.11", {"start": v(22.28, 3.84) * mm, "mid": v(22.06, 3.67) * mm, "end": v(22, 3.41) * mm});
            skLineSegment(sketch, "E38.11.12", {"start": v(27.54, 7.77) * mm, "end": v(27.5, 7.94) * mm});
            skArc(sketch, "E38.11.13", {"start": v(27.53, 7.52) * mm, "mid": v(27.56, 7.64) * mm, "end": v(27.54, 7.77) * mm});
            skLineSegment(sketch, "E38.12.0", {"start": v(18.24, 17.72) * mm, "end": v(16.01, 15.94) * mm});
            skPoint(sketch, "E38.12.1", {"position": v(15.75, 15.73) * mm});
            skLineSegment(sketch, "E38.12.2", {"start": v(21.35, 13.83) * mm, "end": v(19.12, 12.05) * mm});
            skPoint(sketch, "E38.12.3", {"position": v(22.18, 18.07) * mm});
            skArc(sketch, "E38.12.4", {"start": v(18.24, 17.72) * mm, "mid": v(20.11, 18.2) * mm, "end": v(22.05, 18.1) * mm});
            skPoint(sketch, "E38.12.5", {"position": v(18.85, 11.84) * mm});
            skArc(sketch, "E38.12.6", {"start": v(21.35, 13.83) * mm, "mid": v(22.23, 15.55) * mm, "end": v(22.56, 17.46) * mm});
            skPoint(sketch, "E38.12.7", {"position": v(22.56, 17.6) * mm});
            skArc(sketch, "E38.12.8", {"start": v(22.26, 17.97) * mm, "mid": v(22.17, 18.06) * mm, "end": v(22.05, 18.1) * mm});
            skLineSegment(sketch, "E38.12.9", {"start": v(22.26, 17.97) * mm, "end": v(22.37, 17.84) * mm});
            skArc(sketch, "E38.12.10", {"start": v(15.5, 15.97) * mm, "mid": v(15.75, 15.86) * mm, "end": v(16.01, 15.94) * mm});
            skArc(sketch, "E38.12.11", {"start": v(19.12, 12.05) * mm, "mid": v(18.98, 11.82) * mm, "end": v(19.03, 11.56) * mm});
            skLineSegment(sketch, "E38.12.12", {"start": v(22.48, 17.7) * mm, "end": v(22.37, 17.84) * mm});
            skArc(sketch, "E38.12.13", {"start": v(22.56, 17.46) * mm, "mid": v(22.54, 17.59) * mm, "end": v(22.48, 17.7) * mm});
            skLineSegment(sketch, "E38.13.0", {"start": v(10.07, 23.34) * mm, "end": v(8.7, 20.84) * mm});
            skPoint(sketch, "E38.13.1", {"position": v(8.53, 20.54) * mm});
            skLineSegment(sketch, "E38.13.2", {"start": v(14.43, 20.93) * mm, "end": v(13.05, 18.43) * mm});
            skPoint(sketch, "E38.13.3", {"position": v(13.58, 25.17) * mm});
            skArc(sketch, "E38.13.4", {"start": v(10.07, 23.34) * mm, "mid": v(11.62, 24.5) * mm, "end": v(13.44, 25.14) * mm});
            skPoint(sketch, "E38.13.5", {"position": v(12.9, 18.14) * mm});
            skArc(sketch, "E38.13.6", {"start": v(14.43, 20.93) * mm, "mid": v(14.6, 22.86) * mm, "end": v(14.16, 24.75) * mm});
            skPoint(sketch, "E38.13.7", {"position": v(14.11, 24.87) * mm});
            skArc(sketch, "E38.13.8", {"start": v(13.7, 25.1) * mm, "mid": v(13.57, 25.15) * mm, "end": v(13.44, 25.14) * mm});
            skLineSegment(sketch, "E38.13.9", {"start": v(13.7, 25.1) * mm, "end": v(13.85, 25.02) * mm});
            skArc(sketch, "E38.13.10", {"start": v(8.22, 20.67) * mm, "mid": v(8.49, 20.66) * mm, "end": v(8.7, 20.84) * mm});
            skArc(sketch, "E38.13.11", {"start": v(13.05, 18.43) * mm, "mid": v(13.02, 18.17) * mm, "end": v(13.16, 17.94) * mm});
            skLineSegment(sketch, "E38.13.12", {"start": v(14, 24.94) * mm, "end": v(13.85, 25.02) * mm});
            skArc(sketch, "E38.13.13", {"start": v(14.16, 24.75) * mm, "mid": v(14.1, 24.86) * mm, "end": v(14, 24.94) * mm});
            skLineSegment(sketch, "E38.14.0", {"start": v(0.38, 25.4) * mm, "end": v(0.06, 22.56) * mm});
            skPoint(sketch, "E38.14.1", {"position": v(0.02, 22.22) * mm});
            skLineSegment(sketch, "E38.14.2", {"start": v(5.33, 24.84) * mm, "end": v(5.01, 22) * mm});
            skPoint(sketch, "E38.14.3", {"position": v(2.92, 28.43) * mm});
            skArc(sketch, "E38.14.4", {"start": v(0.38, 25.4) * mm, "mid": v(1.36, 27.06) * mm, "end": v(2.8, 28.36) * mm});
            skPoint(sketch, "E38.14.5", {"position": v(4.97, 21.67) * mm});
            skArc(sketch, "E38.14.6", {"start": v(5.33, 24.84) * mm, "mid": v(4.74, 26.69) * mm, "end": v(3.62, 28.27) * mm});
            skPoint(sketch, "E38.14.7", {"position": v(3.52, 28.36) * mm});
            skArc(sketch, "E38.14.8", {"start": v(3.05, 28.42) * mm, "mid": v(2.92, 28.4) * mm, "end": v(2.8, 28.36) * mm});
            skLineSegment(sketch, "E38.14.9", {"start": v(3.05, 28.42) * mm, "end": v(3.22, 28.4) * mm});
            skArc(sketch, "E38.14.10", {"start": v(-0.31, 22.22) * mm, "mid": v(-0.06, 22.32) * mm, "end": v(0.06, 22.56) * mm});
            skArc(sketch, "E38.14.11", {"start": v(5.01, 22) * mm, "mid": v(5.08, 21.75) * mm, "end": v(5.3, 21.6) * mm});
            skLineSegment(sketch, "E38.14.12", {"start": v(3.39, 28.38) * mm, "end": v(3.22, 28.4) * mm});
            skArc(sketch, "E38.14.13", {"start": v(3.62, 28.27) * mm, "mid": v(3.51, 28.34) * mm, "end": v(3.39, 28.38) * mm});
            skLineSegment(sketch, "E38.15.0", {"start": v(-9.37, 23.6) * mm, "end": v(-8.57, 20.85) * mm});
            skPoint(sketch, "E38.15.1", {"position": v(-8.48, 20.52) * mm});
            skLineSegment(sketch, "E38.15.2", {"start": v(-4.58, 24.97) * mm, "end": v(-3.79, 22.23) * mm});
            skPoint(sketch, "E38.15.3", {"position": v(-8.18, 27.36) * mm});
            skArc(sketch, "E38.15.4", {"start": v(-9.37, 23.6) * mm, "mid": v(-9.1, 25.5) * mm, "end": v(-8.26, 27.25) * mm});
            skPoint(sketch, "E38.15.5", {"position": v(-3.7, 21.9) * mm});
            skArc(sketch, "E38.15.6", {"start": v(-4.58, 24.97) * mm, "mid": v(-5.83, 26.45) * mm, "end": v(-7.47, 27.48) * mm});
            skPoint(sketch, "E38.15.7", {"position": v(-7.6, 27.53) * mm});
            skArc(sketch, "E38.15.8", {"start": v(-8.05, 27.4) * mm, "mid": v(-8.17, 27.35) * mm, "end": v(-8.26, 27.25) * mm});
            skLineSegment(sketch, "E38.15.9", {"start": v(-8.05, 27.4) * mm, "end": v(-7.9, 27.45) * mm});
            skArc(sketch, "E38.15.10", {"start": v(-8.79, 20.4) * mm, "mid": v(-8.6, 20.58) * mm, "end": v(-8.57, 20.85) * mm});
            skArc(sketch, "E38.15.11", {"start": v(-3.79, 22.23) * mm, "mid": v(-3.63, 22.02) * mm, "end": v(-3.36, 21.96) * mm});
            skLineSegment(sketch, "E38.15.12", {"start": v(-7.72, 27.5) * mm, "end": v(-7.9, 27.45) * mm});
            skArc(sketch, "E38.15.13", {"start": v(-7.47, 27.48) * mm, "mid": v(-7.6, 27.51) * mm, "end": v(-7.72, 27.5) * mm});
            skArc(sketch, "E39.trimOffspring", {"start": v(-8.48, 20.52) * mm, "mid": v(-10.02, 19.81) * mm, "end": v(-11.5, 18.98) * mm});
            skArc(sketch, "E40.trimOffspring", {"start": v(-20.5, 8.48) * mm, "mid": v(-21.14, 6.73) * mm, "end": v(-21.63, 4.93) * mm});
            skArc(sketch, "E41.trimOffspring", {"start": v(0.02, 22.22) * mm, "mid": v(-1.84, 22.14) * mm, "end": v(-3.7, 21.9) * mm});
            skArc(sketch, "E42.trimOffspring", {"start": v(-22.18, -0.02) * mm, "mid": v(-22.1, -1.89) * mm, "end": v(-21.86, -3.74) * mm});
            skArc(sketch, "E43.trimOffspring", {"start": v(-20.48, -8.53) * mm, "mid": v(-19.77, -10.07) * mm, "end": v(-18.94, -11.56) * mm});
            skArc(sketch, "E44.trimOffspring", {"start": v(8.53, 20.54) * mm, "mid": v(6.78, 21.18) * mm, "end": v(4.97, 21.67) * mm});
            skArc(sketch, "E45.trimOffspring", {"start": v(15.75, 15.73) * mm, "mid": v(14.37, 17) * mm, "end": v(12.9, 18.14) * mm});
            skArc(sketch, "E46.trimOffspring", {"start": v(-15.65, -15.73) * mm, "mid": v(-14.4, -16.89) * mm, "end": v(-13.07, -17.94) * mm});
            skArc(sketch, "E47.trimOffspring", {"start": v(-8.44, -20.54) * mm, "mid": v(-6.68, -21.18) * mm, "end": v(-4.88, -21.67) * mm});
            skArc(sketch, "E48.trimOffspring", {"start": v(8.57, -20.52) * mm, "mid": v(10.27, -19.74) * mm, "end": v(11.89, -18.8) * mm});
            skArc(sketch, "E49.trimOffspring", {"start": v(0.07, -22.22) * mm, "mid": v(1.94, -22.14) * mm, "end": v(3.79, -21.9) * mm});
            skArc(sketch, "E50.trimOffspring", {"start": v(15.78, -15.7) * mm, "mid": v(16.93, -14.45) * mm, "end": v(17.99, -13.12) * mm});
            skArc(sketch, "E51.trimOffspring", {"start": v(20.59, -8.48) * mm, "mid": v(21.18, -6.89) * mm, "end": v(21.64, -5.25) * mm});
            skArc(sketch, "E52.trimOffspring", {"start": v(22.27, 0.02) * mm, "mid": v(22.2, 1.89) * mm, "end": v(21.95, 3.74) * mm});
            skArc(sketch, "E53.trimOffspring", {"start": v(20.57, 8.53) * mm, "mid": v(19.78, 10.22) * mm, "end": v(18.85, 11.84) * mm});
            skSolve(sketch);
        }
        {
            var Q0;
            Q0=makeQuery(id+"F2.imprint","IMPRINT",FACE,{"disambiguationData":[TD([[makeQuery(id+"F2.imprint","IMPRINT",EDGE,{"derivedFrom":sQuery(id+"F2.wireOp",EDGE,"E28.trimOffspring")}),1.0]])]});
            var Q1;
            Q1=makeQuery(id+"F0.imprint","IMPRINT",FACE,{"disambiguationData":[TD([[makeQuery(id+"F0.imprint","IMPRINT",EDGE,{"derivedFrom":sQuery(id+"F0.wireOp",EDGE,"E1.trimOffspring")}),1.0]])]});
            var Q2;
            Q2=sQuery(id+"F2.wireOp",VERTEX,"E38.14.0.start");
            var Q3;
            Q3=sQuery(id+"F0.wireOp",VERTEX,"E11.15.4.start");
            loft(context, id + "F3", {"sheetProfilesArray" : [{ "sheetProfileEntities" : qUnion([Q0]) }, { "sheetProfileEntities" : qUnion([Q1]) }], "matchConnections" : true, "connections" : [{ "connectionEntities" : qUnion([Q2, Q3]), "connectionEdgeQueries" : qUnion([]), "connectionEdgeParameters" : [] }]});
        }
        {
            var Q0;
            Q0=makeQuery(id+"F3.opLoft","CAP_FACE",FACE,{"disambiguationData":[OSD([makeQuery(id+"F2.imprint","IMPRINT",FACE,{"disambiguationData":[TD([[makeQuery(id+"F2.imprint","IMPRINT",EDGE,{"derivedFrom":sQuery(id+"F2.wireOp",EDGE,"E28.trimOffspring")}),1.0]])]})])],"isStart":true});
            var sketch = newSketch(context, id + "F4", { "sketchPlane" : qUnion([Q0])});
            skCircle(sketch, "E54", {"center": v(0, 0) * mm, "radius": 6.35 * mm});
            skSolve(sketch);
        }
        {
            var Q0;
            Q0 = qSketchRegion(id + "F4", true);
            extrude(context, id + "F5", {"entities" : qUnion([Q0]), "operationType" : NewBodyOperationType.REMOVE, "oppositeDirection" : true, "depth" : 50.8 * mm});
        }
    });
